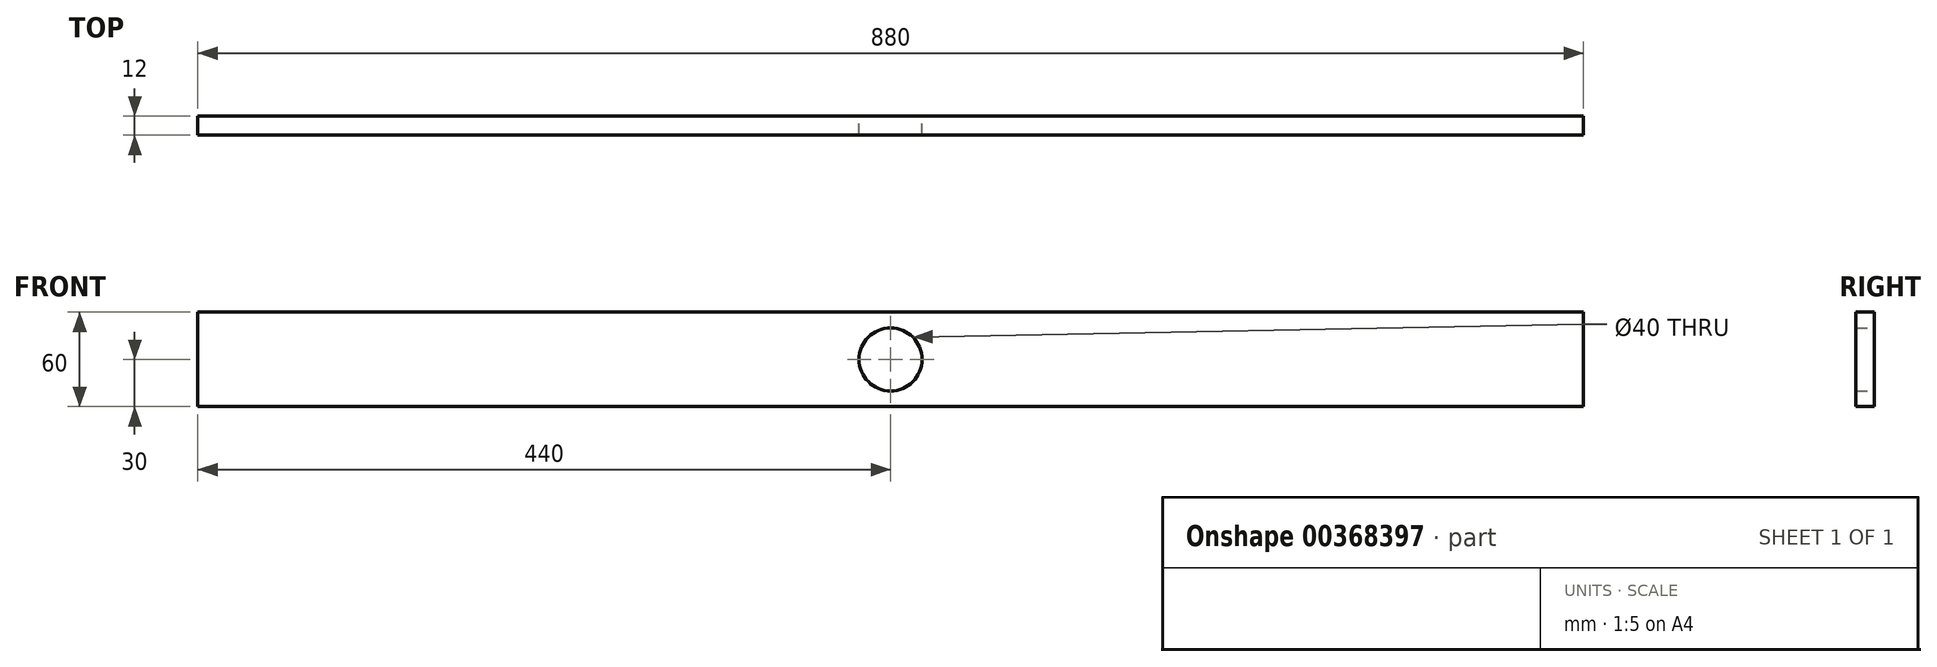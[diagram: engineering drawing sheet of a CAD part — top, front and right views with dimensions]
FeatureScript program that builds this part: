
annotation { "Feature Type Name" : "Feature", "Feature Type Description" : "" }
export const myFeature = defineFeature(function(context is Context, id is Id, definition is map)
    precondition{}
    {
        {
            var Q0;
            Q0=qCreatedBy(makeId("Front.planeOp"),FACE);
            var sketch = newSketch(context, id + "F0", { "sketchPlane" : qUnion([Q0])});
            skLineSegment(sketch, "E0.bottom", {"start": v(-440, 30) * mm, "end": v(440, 30) * mm});
            skLineSegment(sketch, "E0.top", {"start": v(-440, -30) * mm, "end": v(440, -30) * mm});
            skLineSegment(sketch, "E0.left", {"start": v(-440, 30) * mm, "end": v(-440, -30) * mm});
            skLineSegment(sketch, "E0.right", {"start": v(440, 30) * mm, "end": v(440, -30) * mm});
            skPoint(sketch, "E0.middle", {"position": v(0, 0) * mm});
            skCircle(sketch, "E1", {"center": v(0, 0) * mm, "radius": 20 * mm});
            skSolve(sketch);
        }
        {
            var Q0;
            Q0=makeQuery(id+"F0.imprint","IMPRINT",FACE,{"disambiguationData":[TD([[makeQuery(id+"F0.imprint","IMPRINT",EDGE,{"derivedFrom":sQuery(id+"F0.wireOp",EDGE,"E0.bottom")}),-1.0]])]});
            extrude(context, id + "F1", {"entities" : qUnion([Q0]), "depth" : 12 * mm});
        }
    });
